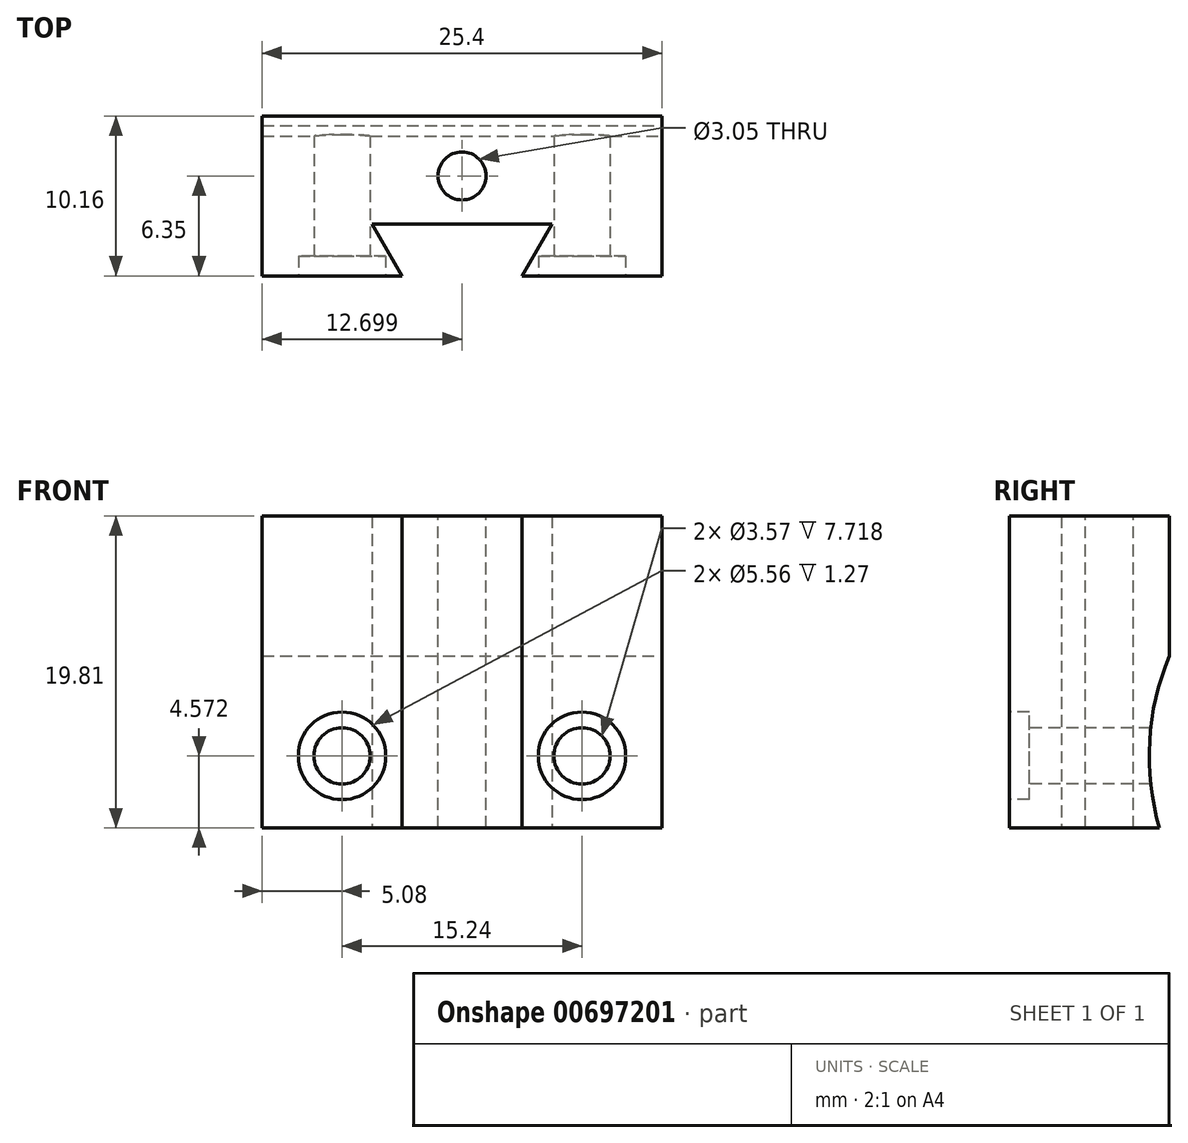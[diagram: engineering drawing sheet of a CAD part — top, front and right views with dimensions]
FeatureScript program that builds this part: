
annotation { "Feature Type Name" : "Feature", "Feature Type Description" : "" }
export const myFeature = defineFeature(function(context is Context, id is Id, definition is map)
    precondition{}
    {
        {
            var Q0;
            Q0=qCreatedBy(makeId("Front.planeOp"),FACE);
            var sketch = newSketch(context, id + "F0", { "sketchPlane" : qUnion([Q0])});
            skLineSegment(sketch, "E0.bottom", {"start": v(0, 19.81) * mm, "end": v(25.4, 19.81) * mm});
            skLineSegment(sketch, "E0.top", {"start": v(0, 0) * mm, "end": v(25.4, 0) * mm});
            skLineSegment(sketch, "E0.left", {"start": v(0, 19.81) * mm, "end": v(0, 0) * mm});
            skLineSegment(sketch, "E0.right", {"start": v(25.4, 19.81) * mm, "end": v(25.4, 0) * mm});
            skSolve(sketch);
        }
        {
            var Q0;
            Q0=makeQuery(id+"F0.imprint","IMPRINT",FACE,{"disambiguationData":[TD([[makeQuery(id+"F0.imprint","IMPRINT",EDGE,{"derivedFrom":sQuery(id+"F0.wireOp",EDGE,"E0.bottom")}),-1.0]])]});
            extrude(context, id + "F1", {"entities" : qUnion([Q0]), "depth" : 10.16 * mm, "offsetDistance" : 25.4 * mm});
        }
        {
            var Q0;
            Q0=makeQuery(id+"F1.opExtrude","CAP_FACE",FACE,{"disambiguationData":[OSD([sQuery(id+"F0.wireOp",EDGE,"E0.bottom"),sQuery(id+"F0.wireOp",EDGE,"E0.top"),sQuery(id+"F0.wireOp",EDGE,"E0.left"),sQuery(id+"F0.wireOp",EDGE,"E0.right")])],"isStart":false});
            var sketch = newSketch(context, id + "F2", { "sketchPlane" : qUnion([Q0])});
            skLineSegment(sketch, "E1", {"start": v(5.08, 0) * mm, "end": v(5.08, 4.57) * mm});
            skLineSegment(sketch, "E2", {"start": v(5.08, 4.57) * mm, "end": v(20.32, 4.57) * mm});
            skLineSegment(sketch, "E3", {"start": v(20.32, 4.57) * mm, "end": v(25.4, 4.57) * mm});
            skLineSegment(sketch, "E4", {"start": v(5.08, 4.57) * mm, "end": v(0, 4.57) * mm});
            skSolve(sketch);
        }
        {
            var Q0;
            Q0=sQuery(id+"F2.wireOp",VERTEX,"E4.start");
            var Q1;
            Q1=makeQuery(id+"F1.opExtrude","SWEPT_BODY",BODY,{"disambiguationData":[OSD([sQuery(id+"F0.wireOp",EDGE,"E0.bottom"),sQuery(id+"F0.wireOp",EDGE,"E0.top"),sQuery(id+"F0.wireOp",EDGE,"E0.left"),sQuery(id+"F0.wireOp",EDGE,"E0.right")])]});
            hole(context, id + "F3", {"style" : HoleStyle.C_BORE, "endStyle" : HoleEndStyle.THROUGH, "holeDiameter" : 3.57 * mm, "cBoreDiameter" : 5.56 * mm, "cBoreDepth" : 1.27 * mm, "majorDiameter" : 6.35 * mm, "isTappedThrough" : true, "tappedDepth" : 12.7 * mm, "tapClearance" : 3, "locations" : qUnion([Q0]), "scope" : qUnion([Q1])});
        }
        {
            var Q0;
            Q0=sQuery(id+"F2.wireOp",VERTEX,"E3.start");
            var Q1;
            Q1=makeQuery(id+"F1.opExtrude","SWEPT_BODY",BODY,{"disambiguationData":[OSD([sQuery(id+"F0.wireOp",EDGE,"E0.bottom"),sQuery(id+"F0.wireOp",EDGE,"E0.top"),sQuery(id+"F0.wireOp",EDGE,"E0.left"),sQuery(id+"F0.wireOp",EDGE,"E0.right")])]});
            hole(context, id + "F4", {"style" : HoleStyle.C_BORE, "endStyle" : HoleEndStyle.THROUGH, "holeDiameter" : 3.57 * mm, "cBoreDiameter" : 5.56 * mm, "cBoreDepth" : 1.27 * mm, "majorDiameter" : 6.35 * mm, "isTappedThrough" : true, "tappedDepth" : 12.7 * mm, "tapClearance" : 3, "locations" : qUnion([Q0]), "scope" : qUnion([Q1])});
        }
        {
            var Q0;
            Q0=makeQuery(id+"F1.opExtrude","SWEPT_FACE",FACE,{"disambiguationData":[OSD([sQuery(id+"F0.wireOp",EDGE,"E0.top")])]});
            var sketch = newSketch(context, id + "F5", { "sketchPlane" : qUnion([Q0])});
            skLineSegment(sketch, "E5", {"start": v(8.9, 10.16) * mm, "end": v(6.98, 6.86) * mm});
            skLineSegment(sketch, "E6", {"start": v(6.98, 6.86) * mm, "end": v(18.41, 6.86) * mm});
            skLineSegment(sketch, "E7", {"start": v(18.41, 6.86) * mm, "end": v(16.5, 10.16) * mm});
            skLineSegment(sketch, "E8", {"start": v(6.98, 6.86) * mm, "end": v(0, 6.86) * mm});
            skSolve(sketch);
        }
        {
            var Q0;
            {var subQ0=sQuery(id+"F5.wireOp",EDGE,"E5");Q0=makeQuery(id+"F5.imprint","IMPRINT",FACE,{"disambiguationData":[TD([[makeQuery(id+"F5.imprint","IMPRINT",EDGE,{"derivedFrom":subQ0}),1.0]])]});}
            extrude(context, id + "F6", {"entities" : qUnion([Q0]), "operationType" : NewBodyOperationType.REMOVE, "endBound" : BoundingType.THROUGH_ALL, "oppositeDirection" : true, "depth" : 25.4 * mm, "offsetDistance" : 25.4 * mm});
        }
        {
            var Q0;
            Q0=makeQuery(id+"F1.opExtrude","SWEPT_FACE",FACE,{"disambiguationData":[OSD([sQuery(id+"F0.wireOp",EDGE,"E0.bottom")])]});
            var sketch = newSketch(context, id + "F7", { "sketchPlane" : qUnion([Q0])});
            skLineSegment(sketch, "E9", {"start": v(12.7, -6.86) * mm, "end": v(12.7, -3.8) * mm});
            skSolve(sketch);
        }
        {
            var Q0;
            Q0=sQuery(id+"F7.wireOp",VERTEX,"E9.end");
            var Q1;
            Q1=makeQuery(id+"F1.opExtrude","SWEPT_BODY",BODY,{"disambiguationData":[OSD([sQuery(id+"F0.wireOp",EDGE,"E0.bottom"),sQuery(id+"F0.wireOp",EDGE,"E0.top"),sQuery(id+"F0.wireOp",EDGE,"E0.left"),sQuery(id+"F0.wireOp",EDGE,"E0.right")])]});
            hole(context, id + "F8", {"style" : HoleStyle.SIMPLE, "endStyle" : HoleEndStyle.THROUGH, "standardTappedOrClearance" : lookupTablePath({ "standard" : "ANSI", "engagement" : "50%", "pitch" : "40 tpi", "size" : "#6", "type" : "Tapped" }), "standardBlindInLast" : lookupTablePath({ "standard" : "ANSI", "engagement" : "50%", "pitch" : "40 tpi", "size" : "#6", "type" : "Tapped" }), "holeDiameter" : 3.05 * mm, "majorDiameter" : 3.5 * mm, "showTappedDepth" : true, "isTappedThrough" : true, "tappedDepth" : 12.7 * mm, "tapClearance" : 3, "locations" : qUnion([Q0]), "scope" : qUnion([Q1])});
        }
        {
            var Q0;
            Q0=makeQuery(id+"F1.opExtrude","SWEPT_FACE",FACE,{"disambiguationData":[OSD([sQuery(id+"F0.wireOp",EDGE,"E0.right")])]});
            var sketch = newSketch(context, id + "F9", { "sketchPlane" : qUnion([Q0])});
            skLineSegment(sketch, "E10", {"start": v(-10.16, 4.57) * mm, "end": v(0, 4.57) * mm});
            skLineSegment(sketch, "E11", {"start": v(-4.7, 4.57) * mm, "end": v(-4.7, 0) * mm});
            skLineSegment(sketch, "E12", {"start": v(0, 4.57) * mm, "end": v(-1.27, 4.57) * mm});
            skLineSegment(sketch, "E13", {"start": v(-1.27, 4.57) * mm, "end": v(31.62, 4.57) * mm});
            skCircle(sketch, "E14", {"center": v(15.18, 4.57) * mm, "radius": 16.45 * mm});
            skSolve(sketch);
        }
        {
            var Q0;
            Q0 = qSketchRegion(id + "F9", true);
            extrude(context, id + "F10", {"entities" : qUnion([Q0]), "operationType" : NewBodyOperationType.REMOVE, "oppositeDirection" : true, "depth" : 25.4 * mm, "offsetDistance" : 25.4 * mm});
        }
    });
